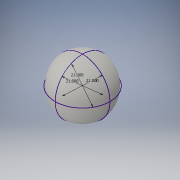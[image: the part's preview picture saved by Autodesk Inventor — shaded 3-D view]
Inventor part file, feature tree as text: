
AUTODESK INVENTOR PART (.ipt)
format: ipt  version: 2016 (Build 200138000, 138)  size: 164,352 bytes
history: native  units: in
note: dims shown in document units (in); Inventor stores cm internally (conversion verified against a paired STEP export)
features: sketch x3, other x1
ambient origin geometry x8: Origin, YZ Plane, XZ Plane, XY Plane, X Axis, Y Axis, Z Axis, Center Point
bodies: Solid3 (feature_tree)
feature tree (4):
  sketch  "Sketch1"  dims[d0=21.0in]
  sketch  "Sketch2"  dims[d1=21.0in]
  sketch  "Sketch3"  dims[d6=21.0in]
  other  "Form1"
